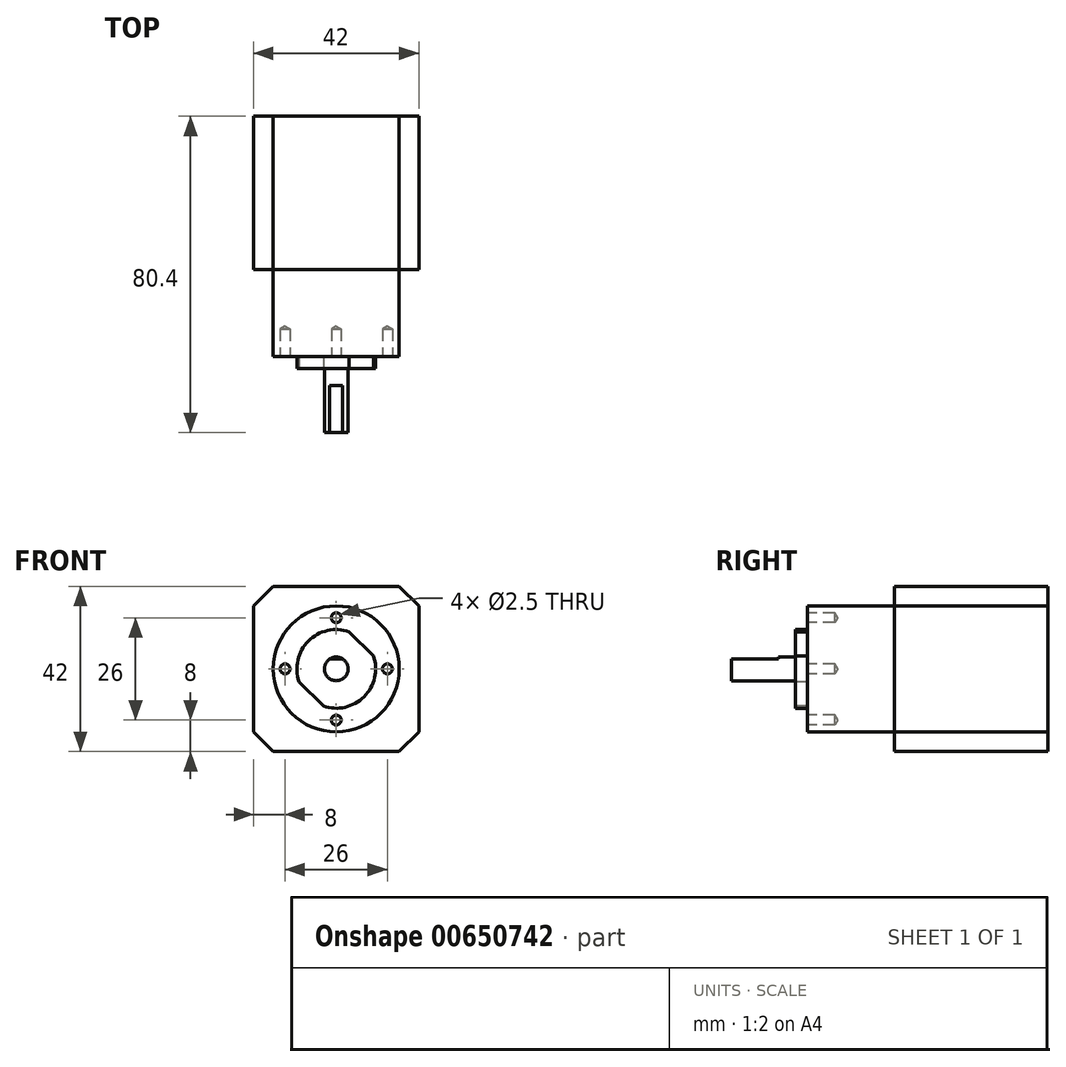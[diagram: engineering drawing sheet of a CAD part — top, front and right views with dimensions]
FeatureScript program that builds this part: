
annotation { "Feature Type Name" : "Feature", "Feature Type Description" : "" }
export const myFeature = defineFeature(function(context is Context, id is Id, definition is map)
    precondition{}
    {
        {
            var Q0;
            Q0=qCreatedBy(makeId("Front.planeOp"),FACE);
            var sketch = newSketch(context, id + "F0", { "sketchPlane" : qUnion([Q0])});
            skLineSegment(sketch, "E0.bottom", {"start": v(-21, 21) * mm, "end": v(21, 21) * mm});
            skLineSegment(sketch, "E0.top", {"start": v(-21, -21) * mm, "end": v(21, -21) * mm});
            skLineSegment(sketch, "E0.left", {"start": v(-21, 21) * mm, "end": v(-21, -21) * mm});
            skLineSegment(sketch, "E0.right", {"start": v(21, 21) * mm, "end": v(21, -21) * mm});
            skPoint(sketch, "E0.middle", {"position": v(0, 0) * mm});
            skSolve(sketch);
        }
        {
            var Q0;
            Q0 = qSketchRegion(id + "F0", true);
            extrude(context, id + "F1", {"entities" : qUnion([Q0]), "depth" : 39 * mm, "offsetDistance" : 25 * mm});
        }
        {
            var Q0;
            Q0=makeQuery(id+"F1.opExtrude","CAP_FACE",FACE,{"disambiguationData":[OSD([sQuery(id+"F0.wireOp",EDGE,"E0.bottom"),sQuery(id+"F0.wireOp",EDGE,"E0.top"),sQuery(id+"F0.wireOp",EDGE,"E0.left"),sQuery(id+"F0.wireOp",EDGE,"E0.right")])],"isStart":false});
            var sketch = newSketch(context, id + "F2", { "sketchPlane" : qUnion([Q0])});
            skCircle(sketch, "E1", {"center": v(0, 0) * mm, "radius": 16 * mm});
            skSolve(sketch);
        }
        {
            var Q0;
            Q0 = qSketchRegion(id + "F2", true);
            extrude(context, id + "F3", {"entities" : qUnion([Q0]), "operationType" : NewBodyOperationType.ADD, "depth" : 22.1 * mm, "offsetDistance" : 25 * mm});
        }
        {
            var Q0;
            Q0=makeQuery(id+"F3.opExtrude","CAP_FACE",FACE,{"disambiguationData":[OSD([sQuery(id+"F2.wireOp",EDGE,"E1")])],"isStart":false});
            var sketch = newSketch(context, id + "F4", { "sketchPlane" : qUnion([Q0])});
            skCircle(sketch, "E2", {"center": v(0, 0) * mm, "radius": 10 * mm});
            skSolve(sketch);
        }
        {
            var Q0;
            Q0 = qSketchRegion(id + "F4", true);
            extrude(context, id + "F5", {"entities" : qUnion([Q0]), "operationType" : NewBodyOperationType.ADD, "depth" : 3 * mm, "offsetDistance" : 25 * mm});
        }
        {
            var Q0;
            Q0=makeQuery(id+"F5.opExtrude","CAP_FACE",FACE,{"disambiguationData":[OSD([sQuery(id+"F4.wireOp",EDGE,"E2")])],"isStart":false});
            var sketch = newSketch(context, id + "F6", { "sketchPlane" : qUnion([Q0])});
            skCircle(sketch, "E3", {"center": v(0, 0) * mm, "radius": 3 * mm});
            skSolve(sketch);
        }
        {
            var Q0;
            Q0 = qSketchRegion(id + "F6", true);
            extrude(context, id + "F7", {"entities" : qUnion([Q0]), "operationType" : NewBodyOperationType.ADD, "depth" : 16.3 * mm, "offsetDistance" : 25 * mm});
        }
        {
            var Q0;
            Q0=makeQuery(id+"F1.opExtrude","SWEPT_EDGE",EDGE,{"disambiguationData":[OSD([sQuery(id+"F0.wireOp",EDGE,"E0.bottom"),sQuery(id+"F0.wireOp",EDGE,"E0.left")])]});
            var Q1;
            Q1=makeQuery(id+"F1.opExtrude","SWEPT_EDGE",EDGE,{"disambiguationData":[OSD([sQuery(id+"F0.wireOp",EDGE,"E0.bottom"),sQuery(id+"F0.wireOp",EDGE,"E0.right")])]});
            var Q2;
            Q2=makeQuery(id+"F1.opExtrude","SWEPT_EDGE",EDGE,{"disambiguationData":[OSD([sQuery(id+"F0.wireOp",EDGE,"E0.top"),sQuery(id+"F0.wireOp",EDGE,"E0.right")])]});
            var Q3;
            Q3=makeQuery(id+"F1.opExtrude","SWEPT_EDGE",EDGE,{"disambiguationData":[OSD([sQuery(id+"F0.wireOp",EDGE,"E0.top"),sQuery(id+"F0.wireOp",EDGE,"E0.left")])]});
            chamfer(context, id + "F8", {"entities" : qUnion([Q0, Q1, Q2, Q3]), "width" : 5 * mm, "tangentPropagation" : true});
        }
        {
            var Q0;
            Q0=makeQuery(id+"F7.opExtrude","CAP_FACE",FACE,{"disambiguationData":[OSD([sQuery(id+"F6.wireOp",EDGE,"E3")])],"isStart":false});
            var sketch = newSketch(context, id + "F9", { "sketchPlane" : qUnion([Q0])});
            skCircle(sketch, "E4.0", {"center": v(0, 0) * mm, "radius": 3 * mm});
            skLineSegment(sketch, "E5", {"start": v(-1.66, 2.5) * mm, "end": v(1.66, 2.5) * mm});
            skSolve(sketch);
        }
        {
            var Q0;
            {var subQ0=sQuery(id+"F9.wireOp",EDGE,"E5");Q0=makeQuery(id+"F9.imprint","IMPRINT",FACE,{"disambiguationData":[TD([[makeQuery(id+"F9.imprint","IMPRINT",EDGE,{"derivedFrom":subQ0}),1.0]])]});}
            extrude(context, id + "F10", {"entities" : qUnion([Q0]), "operationType" : NewBodyOperationType.REMOVE, "oppositeDirection" : true, "depth" : 12 * mm, "offsetDistance" : 25 * mm});
        }
        {
            var Q0;
            Q0=makeQuery(id+"F5.opExtrude","CAP_FACE",FACE,{"disambiguationData":[OSD([sQuery(id+"F4.wireOp",EDGE,"E2")])],"isStart":false});
            var sketch = newSketch(context, id + "F11", { "sketchPlane" : qUnion([Q0])});
            skCircle(sketch, "E6.0", {"center": v(0, 0) * mm, "radius": 10 * mm});
            skLineSegment(sketch, "E7", {"start": v(3.28, 9.45) * mm, "end": v(9.45, 3.28) * mm});
            skLineSegment(sketch, "E8", {"start": v(-9.45, -3.28) * mm, "end": v(-3.28, -9.45) * mm});
            skLineSegment(sketch, "E9", {"start": v(-26.7, 0) * mm, "end": v(26.3, 0) * mm, "construction": true});
            skLineSegment(sketch, "E10", {"start": v(-6.36, -6.36) * mm, "end": v(6.36, 6.36) * mm, "construction": true});
            skSolve(sketch);
        }
        {
            var Q0;
            {var subQ0=sQuery(id+"F11.wireOp",EDGE,"E7");Q0=makeQuery(id+"F11.imprint","IMPRINT",FACE,{"disambiguationData":[TD([[makeQuery(id+"F11.imprint","IMPRINT",EDGE,{"derivedFrom":subQ0}),1.0]])]});}
            var Q1;
            {var subQ0=sQuery(id+"F11.wireOp",EDGE,"E8");Q1=makeQuery(id+"F11.imprint","IMPRINT",FACE,{"disambiguationData":[TD([[makeQuery(id+"F11.imprint","IMPRINT",EDGE,{"derivedFrom":subQ0}),-1.0]])]});}
            var Q2;
            Q2=makeQuery(id+"F3.opExtrude","CAP_FACE",FACE,{"disambiguationData":[OSD([sQuery(id+"F2.wireOp",EDGE,"E1")])],"isStart":false});
            extrude(context, id + "F12", {"entities" : qUnion([Q0, Q1]), "operationType" : NewBodyOperationType.REMOVE, "endBound" : BoundingType.UP_TO_SURFACE, "oppositeDirection" : true, "depth" : 25 * mm, "endBoundEntityFace" : qUnion([Q2]), "offsetDistance" : 25 * mm});
        }
        {
            var Q0;
            {var subQ0=sQuery(id+"F2.wireOp",EDGE,"E1");Q0=makeQuery(id+"F12.boolean.opBoolean","MERGE",FACE,{"derivedFrom":[makeQuery(id+"F3.opExtrude","CAP_FACE",FACE,{"disambiguationData":[OSD([subQ0])],"isStart":false}),makeQuery(id+"F12.opExtrude","CAP_FACE",FACE,{"disambiguationData":[OSD([subQ0]),OD(0.0)],"isStart":false}),makeQuery(id+"F12.opExtrude","CAP_FACE",FACE,{"disambiguationData":[OSD([subQ0]),OD(1.0)],"isStart":false})]});}
            var sketch = newSketch(context, id + "F13", { "sketchPlane" : qUnion([Q0])});
            skCircle(sketch, "E11", {"center": v(0, 0) * mm, "radius": 13 * mm, "construction": true});
            skPoint(sketch, "E12", {"position": v(13, 0) * mm});
            skPoint(sketch, "E13", {"position": v(-13, 0) * mm});
            skPoint(sketch, "E14", {"position": v(0, 13) * mm});
            skPoint(sketch, "E15", {"position": v(0, -13) * mm});
            skSolve(sketch);
        }
        {
            var Q0;
            Q0=sQuery(id+"F13.wireOp",VERTEX,"E14");
            var Q1;
            Q1=sQuery(id+"F13.wireOp",VERTEX,"E13");
            var Q2;
            Q2=sQuery(id+"F13.wireOp",VERTEX,"E15");
            var Q3;
            Q3=sQuery(id+"F13.wireOp",VERTEX,"E12");
            var Q4;
            Q4=makeQuery(id+"F1.opExtrude","SWEPT_BODY",BODY,{"disambiguationData":[OSD([sQuery(id+"F0.wireOp",EDGE,"E0.bottom"),sQuery(id+"F0.wireOp",EDGE,"E0.top"),sQuery(id+"F0.wireOp",EDGE,"E0.left"),sQuery(id+"F0.wireOp",EDGE,"E0.right")])]});
            hole(context, id + "F14", {"style" : HoleStyle.SIMPLE, "endStyle" : HoleEndStyle.BLIND, "standardTappedOrClearance" : lookupTablePath({ "standard" : "ISO", "engagement" : "75%", "pitch" : "0.5 mm", "size" : "M3", "type" : "Tapped" }), "standardBlindInLast" : lookupTablePath({ "standard" : "ISO", "engagement" : "75%", "pitch" : "0.5 mm", "size" : "M3", "type" : "Tapped" }), "holeDiameter" : 2.5 * mm, "majorDiameter" : 3 * mm, "showTappedDepth" : true, "holeDepth" : 7 * mm, "isTappedThrough" : true, "tappedDepth" : 5.5 * mm, "tapClearance" : 3, "locations" : qUnion([Q0, Q1, Q2, Q3]), "scope" : qUnion([Q4])});
        }
    });
